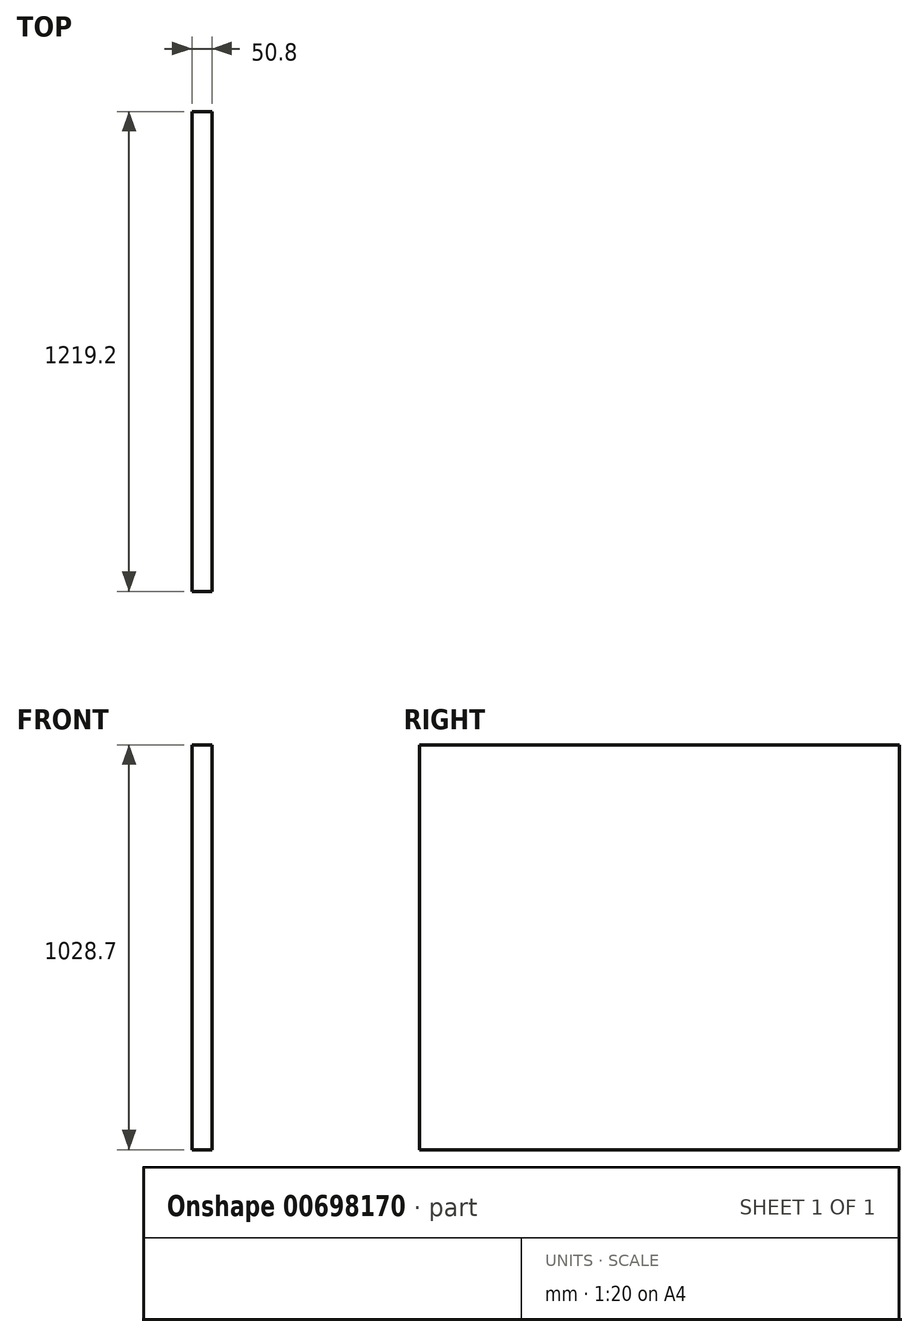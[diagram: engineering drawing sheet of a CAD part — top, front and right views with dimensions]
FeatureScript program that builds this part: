
annotation { "Feature Type Name" : "Feature", "Feature Type Description" : "" }
export const myFeature = defineFeature(function(context is Context, id is Id, definition is map)
    precondition{}
    {
        {
            var Q0;
            Q0=qCreatedBy(makeId("Right.planeOp"),FACE);
            var sketch = newSketch(context, id + "F0", { "sketchPlane" : qUnion([Q0])});
            skLineSegment(sketch, "E0.bottom", {"start": v(609.6, 514.35) * mm, "end": v(-609.6, 514.35) * mm});
            skLineSegment(sketch, "E0.top", {"start": v(609.6, -514.35) * mm, "end": v(-609.6, -514.35) * mm});
            skLineSegment(sketch, "E0.left", {"start": v(609.6, 514.35) * mm, "end": v(609.6, -514.35) * mm});
            skLineSegment(sketch, "E0.right", {"start": v(-609.6, 514.35) * mm, "end": v(-609.6, -514.35) * mm});
            skPoint(sketch, "E0.middle", {"position": v(0, 0) * mm});
            skSolve(sketch);
        }
        {
            var Q0;
            Q0=makeQuery(id+"F0.imprint","IMPRINT",FACE,{"disambiguationData":[TD([[makeQuery(id+"F0.imprint","IMPRINT",EDGE,{"derivedFrom":sQuery(id+"F0.wireOp",EDGE,"E0.bottom")}),1.0]])]});
            extrude(context, id + "F1", {"entities" : qUnion([Q0]), "depth" : 50.8 * mm, "offsetDistance" : 25.4 * mm});
        }
    });
